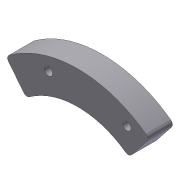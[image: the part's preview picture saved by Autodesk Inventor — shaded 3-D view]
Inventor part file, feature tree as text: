
AUTODESK INVENTOR PART (.ipt)
format: ipt  version: 2012 (Build 160160000, 160)  size: 98,304 bytes
history: native  units: in
note: dims shown in document units (in); Inventor stores cm internally (conversion verified against a paired STEP export)
features: extrude x1, sketch x1
ambient origin geometry x8: Origin, YZ Plane, XZ Plane, XY Plane, X Axis, Y Axis, Z Axis, Center Point
bodies: Solid1 (feature_tree)
feature tree (2):
  extrude  "Extrusion1"  Depth=3.5in
  sketch  "Sketch1"  dims[d0=3.125in d1=3.5in d2=45.0deg d5=0.125in d6=0.75in d7=0.0in d8=0.25in d9=2.5in d10=0.1512in d11=0.0687in]
